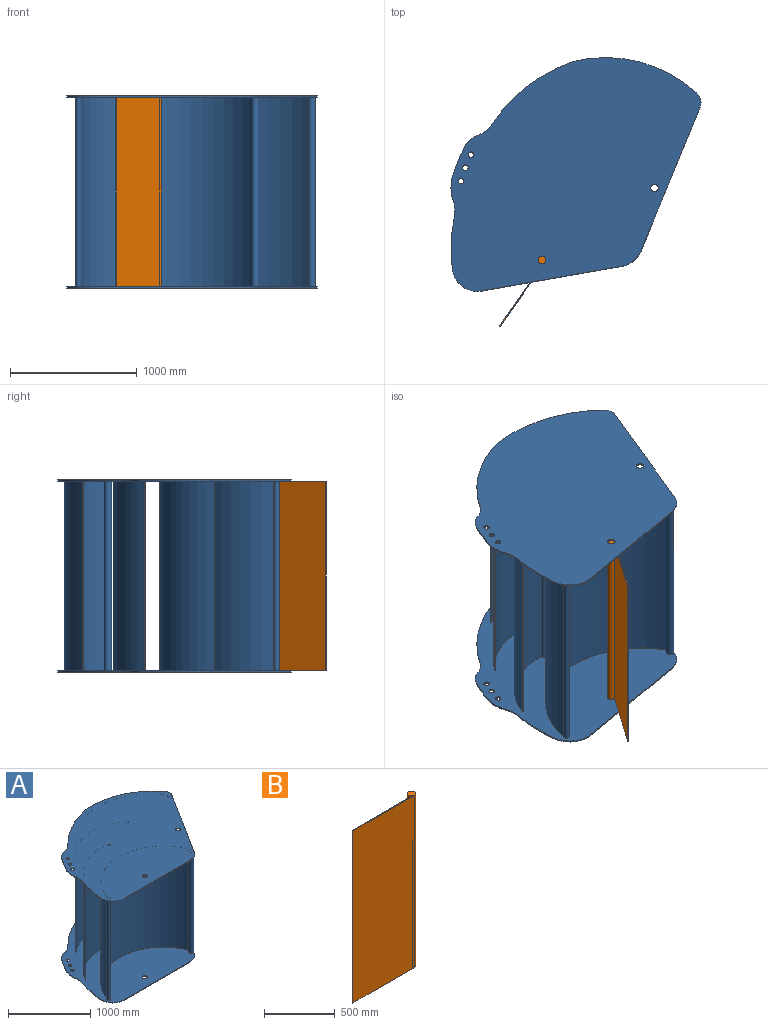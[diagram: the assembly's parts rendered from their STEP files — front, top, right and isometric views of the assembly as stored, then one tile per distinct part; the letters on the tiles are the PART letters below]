
ASSEMBLY  parts=2 mates=2
PART A: 61 faces, bbox 2164.2x1661x1520 mm
  f0: cylinder r=30.5mm len=61mm, axis (0,0,-1), area 1916.4mm2, adj f48,f49
  f1: cylinder r=29.5mm len=59mm, axis (0,0,-1), area 1853.5mm2, adj f48,f49
  f2: cylinder r=22mm len=44mm, axis (0,0,-1), area 1382.3mm2, adj f48,f49
  f3: cylinder r=22mm len=44mm, axis (0,0,-1), area 1382.3mm2, adj f48,f49
  f4: cylinder r=22mm len=44mm, axis (0,0,-1), area 1382.3mm2, adj f48,f49
  f5: cylinder r=326.18mm len=176.61mm, axis (0,0,-1), area 1797.7mm2, adj f48,f49,f50,f60
  f6: cylinder r=200mm len=212.82mm, axis (0,0,-1), area 3269.9mm2, adj f48,f49,f51,f52
  f7: cylinder r=20.5mm len=1500mm, axis (0,0,-1), area 183146.8mm2, adj f30,f44,f45,f49
  f8: cylinder r=30.5mm len=1500mm, axis (0,0,-1), area 272705.4mm2, adj f30,f44,f45,f46,f47,f49
  f9: cylinder r=15.5mm len=1500mm, axis (0,0,-1), area 135747.8mm2, adj f30,f41,f43,f49
  f10: cylinder r=15.5mm len=1500mm, axis (0,0,-1), area 136340.4mm2, adj f30,f37,f40,f49
  f11: cylinder r=30.5mm len=1500mm, axis (0,0,-1), area 274743.1mm2, adj f30,f32,f34,f35,f36,f49
  f12: cylinder r=30.5mm len=61mm, axis (0,0,-1), area 1916.4mm2, adj f30,f31
  f13: cylinder r=22mm len=44mm, axis (0,0,-1), area 1382.3mm2, adj f30,f31
  f14: cylinder r=22mm len=44mm, axis (0,0,-1), area 1382.3mm2, adj f30,f31
  f15: cylinder r=22mm len=44mm, axis (0,0,-1), area 1382.3mm2, adj f30,f31
  f16: cylinder r=29.5mm len=59mm, axis (0,0,-1), area 1853.5mm2, adj f30,f31
  f17: cylinder r=326.18mm len=176.61mm, axis (0,0,-1), area 1797.7mm2, adj f28,f29,f30,f31
  f18: cylinder r=200mm len=212.82mm, axis (0,0,-1), area 3269.9mm2, adj f19,f20,f30,f31
  f19: cylinder r=1403.06mm len=415.74mm, axis (0,0,-1), area 4273.2mm2, adj f18,f29,f30,f31
  f20: plane 1123.76x10mm, normal (0,-1,0), area 11237.6mm2, adj f18,f21,f30,f31
  f21: cylinder r=200mm len=169mm, axis (0,0,-1), area 2013.2mm2, adj f20,f22,f30,f31
  f22: plane 1036.5x655.9mm, normal (0.85,-0.53,0), area 12265.9mm2, adj f21,f23,f30,f31,f36,f47
  f23: cylinder r=100mm len=114.68mm, axis (0,0,-1), area 1222.9mm2, adj f22,f24,f30,f31
  f24: cylinder r=1074.34mm len=926.41mm, axis (0,0,-1), area 10568mm2, adj f23,f25,f30,f31
  f25: cylinder r=1282.61mm len=713.26mm, axis (0,0,-1), area 8227.7mm2, adj f24,f26,f30,f31
  f26: cylinder r=200mm len=117.51mm, axis (0,0,-1), area 1346.6mm2, adj f25,f27,f30,f31
  f27: cylinder r=186.95mm len=116.81mm, axis (0,0,-1), area 1363.1mm2, adj f26,f28,f30,f31
  f28: cylinder r=1324.47mm len=239.75mm, axis (0,0,-1), area 2828.3mm2, adj f17,f27,f30,f31
  f29: cylinder r=200mm len=107.43mm, axis (0,0,-1), area 1093.1mm2, adj f17,f19,f30,f31
  f30: plane 2164.16x1660.98mm, normal (0,0,1), area 2565292.9mm2, adj f7,f8,f9,f10,f11,f12,f13,f14
  f31: plane 2164.16x1660.98mm, normal (0,0,-1), area 2603609.2mm2, adj f12,f13,f14,f15,f16,f17,f18,f19
  f32: cylinder r=883.17mm len=1500mm, axis (0,0,-1), area 1936048.7mm2, adj f11,f30,f33,f49
  f33: plane 1500x5.5mm, normal (-0.92,-0.4,0), area 9000mm2, adj f30,f32,f34,f49
  f34: cylinder r=877.17mm len=1500mm, axis (0,0,-1), area 1914005.6mm2, adj f11,f30,f33,f49
  f35: plane 9.3x5.88mm, normal (0,0,1), area 3.7mm2, adj f11,f54
  f36: plane 9.3x5.88mm, normal (0,0,-1), area 3.7mm2, adj f11,f22
  f37: cylinder r=685.89mm len=1500mm, axis (0,0,-1), area 1444091.5mm2, adj f10,f30,f38,f49
  f38: plane 1500x4.62mm, normal (-0.77,-0.64,0), area 9000mm2, adj f30,f37,f39,f49
  f39: plane 1500x0.08mm, normal (0.65,-0.76,0), area 152.6mm2, adj f30,f38,f40,f49
  f40: cylinder r=679.89mm len=1500mm, axis (0,0,-1), area 1427930.9mm2, adj f10,f30,f39,f49
  f41: cylinder r=640.37mm len=1500mm, axis (0,0,-1), area 1242581.2mm2, adj f9,f30,f42,f49
  f42: plane 1500x5.24mm, normal (-0.49,-0.87,0), area 9000mm2, adj f30,f41,f43,f49
  f43: cylinder r=634.37mm len=1500mm, axis (0,0,-1), area 1226053.6mm2, adj f9,f30,f42,f49
  f44: cylinder r=755.25mm len=1500mm, axis (0,0,-1), area 2799788.5mm2, adj f7,f8,f30,f49
  f45: cylinder r=761.25mm len=1500mm, axis (0,0,-1), area 2838096.4mm2, adj f7,f8,f30,f49
  f46: plane 9.3x5.88mm, normal (0,0,1), area 3.7mm2, adj f8,f54
  f47: plane 9.3x5.88mm, normal (0,0,-1), area 3.7mm2, adj f8,f22
  f48: plane 2164.16x1660.98mm, normal (0,0,1), area 2603609.2mm2, adj f0,f1,f2,f3,f4,f5,f6,f50
  f49: plane 2164.16x1660.98mm, normal (0,0,-1), area 2565292.9mm2, adj f0,f1,f2,f3,f4,f5,f6,f7
  f50: cylinder r=200mm len=107.43mm, axis (0,0,-1), area 1093.1mm2, adj f5,f48,f49,f51
  f51: cylinder r=1403.06mm len=415.74mm, axis (0,0,-1), area 4273.2mm2, adj f6,f48,f49,f50
  f52: plane 1123.76x10mm, normal (0,-1,0), area 11237.6mm2, adj f6,f48,f49,f53
  f53: cylinder r=200mm len=169mm, axis (0,0,-1), area 2013.2mm2, adj f48,f49,f52,f54
  f54: plane 1036.5x655.9mm, normal (0.85,-0.53,0), area 12265.9mm2, adj f35,f46,f48,f49,f53,f55
  f55: cylinder r=100mm len=114.68mm, axis (0,0,-1), area 1222.9mm2, adj f48,f49,f54,f56
  f56: cylinder r=1074.34mm len=926.41mm, axis (0,0,-1), area 10568mm2, adj f48,f49,f55,f57
  f57: cylinder r=1282.61mm len=713.26mm, axis (0,0,-1), area 8227.7mm2, adj f48,f49,f56,f58
  f58: cylinder r=200mm len=117.51mm, axis (0,0,-1), area 1346.6mm2, adj f48,f49,f57,f59
  f59: cylinder r=186.95mm len=116.81mm, axis (0,0,-1), area 1363.1mm2, adj f48,f49,f58,f60
  f60: cylinder r=1324.47mm len=239.75mm, axis (0,0,-1), area 2828.3mm2, adj f5,f48,f49,f59
PART B: 6 faces, bbox 646.3x61x1490 mm
  f0: cylinder r=30.5mm len=1490mm, axis (0,0,-1), area 256544.7mm2, adj f1,f2,f4,f5
  f1: plane 1490x615.77mm, normal (0,-1,0), area 917501.9mm2, adj f0,f3,f4,f5
  f2: plane 1490x597.61mm, normal (0,1,0), area 890434.7mm2, adj f0,f3,f4,f5
  f3: plane 1490x6mm, normal (-1,0,0), area 8940mm2, adj f1,f2,f4,f5
  f4: plane 646.27x61mm, normal (0,0,1), area 6542.9mm2, adj f0,f1,f2,f3
  f5: plane 646.27x61mm, normal (0,0,-1), area 6542.9mm2, adj f0,f1,f2,f3
PLACE A rot(axis=(0,0,1),10deg) t=(0,0,-10)mm
PLACE B rot(axis=(0,0,1),55deg) t=(-664.29,462.04,-10)mm
MATE planar A.f0 <-> B.f0  axis (0,0,-1) through (-889.87,-570.86,750)mm
MATE revolute A.f0 <-> B.f0  axis (0,0,-1) through (-889.87,-570.86,750)mm
